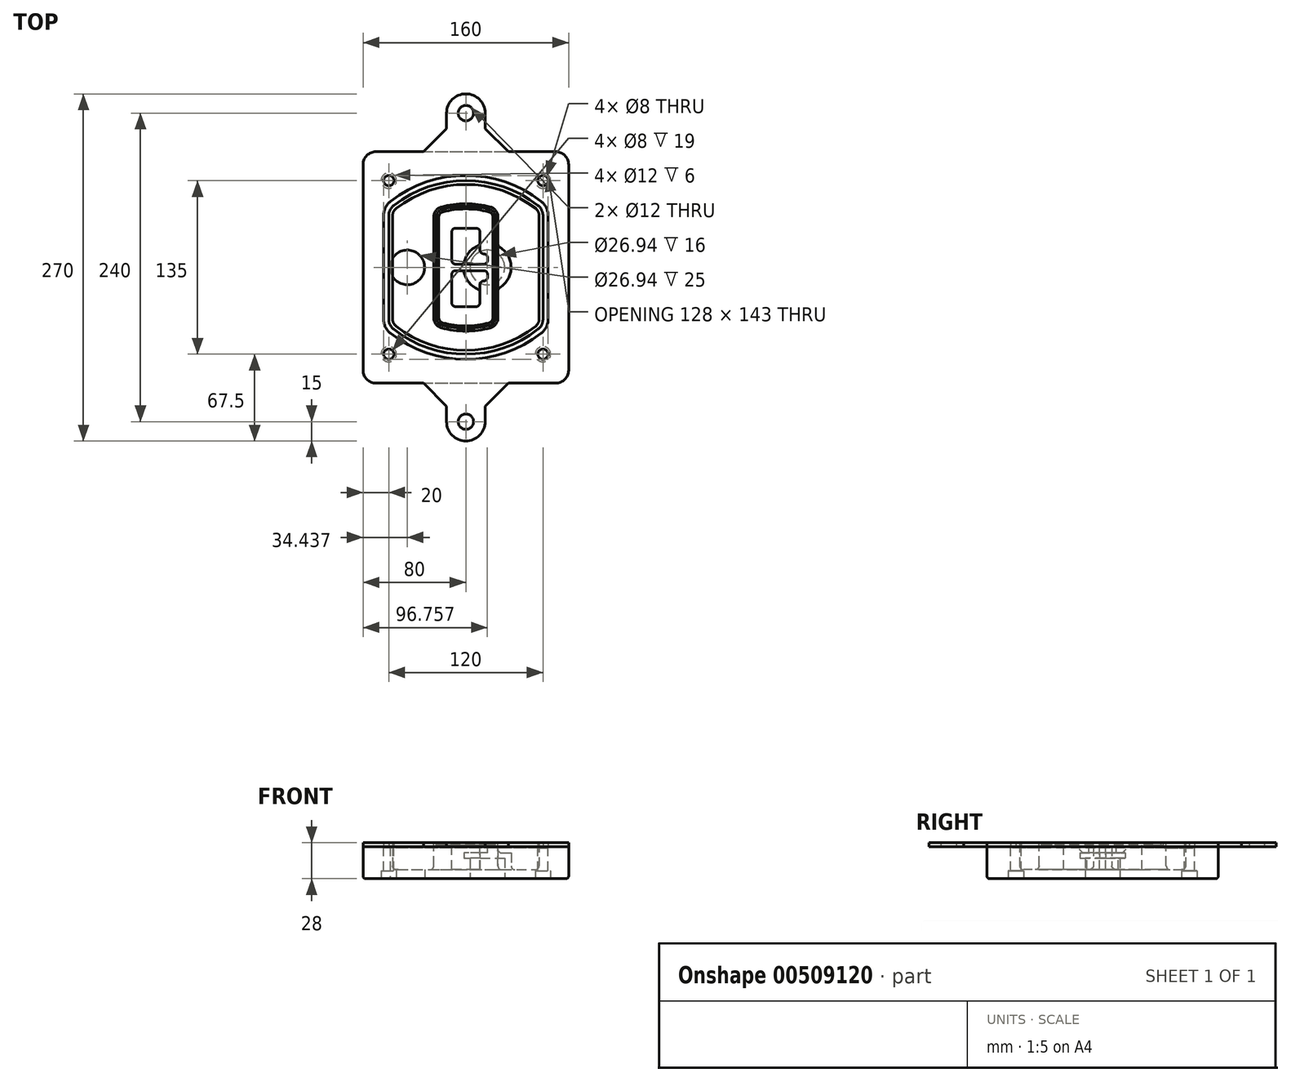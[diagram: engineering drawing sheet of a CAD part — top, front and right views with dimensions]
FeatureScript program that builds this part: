
annotation { "Feature Type Name" : "Feature", "Feature Type Description" : "" }
export const myFeature = defineFeature(function(context is Context, id is Id, definition is map)
    precondition{}
    {
        {
            var Q0;
            Q0=qCreatedBy(makeId("Top.planeOp"),FACE);
            var sketch = newSketch(context, id + "F0", { "sketchPlane" : qUnion([Q0])});
            skPoint(sketch, "E0.rect.middle", {"position": v(0, 0) * mm});
            skLineSegment(sketch, "E1.bottom", {"start": v(-70, -90) * mm, "end": v(70, -90) * mm});
            skLineSegment(sketch, "E1.top", {"start": v(-70, 90) * mm, "end": v(70, 90) * mm});
            skLineSegment(sketch, "E1.left", {"start": v(-80, -80) * mm, "end": v(-80, 80) * mm});
            skLineSegment(sketch, "E1.right", {"start": v(80, -80) * mm, "end": v(80, 80) * mm});
            skLineSegment(sketch, "E2", {"start": v(-80, 90) * mm, "end": v(80, -90) * mm, "construction": true});
            skLineSegment(sketch, "E3", {"start": v(80, 90) * mm, "end": v(-80, -90) * mm, "construction": true});
            skCircle(sketch, "E4", {"center": v(-60, 67.5) * mm, "radius": 4 * mm});
            skCircle(sketch, "E5", {"center": v(60, 67.5) * mm, "radius": 4 * mm});
            skCircle(sketch, "E6", {"center": v(60, -67.5) * mm, "radius": 4 * mm});
            skCircle(sketch, "E7", {"center": v(-60, -67.5) * mm, "radius": 4 * mm});
            skLineSegment(sketch, "E8", {"start": v(-60, 67.5) * mm, "end": v(60, 67.5) * mm, "construction": true});
            skLineSegment(sketch, "E9", {"start": v(60, 67.5) * mm, "end": v(60, -67.5) * mm, "construction": true});
            skLineSegment(sketch, "E10", {"start": v(60, -67.5) * mm, "end": v(-60, -67.5) * mm, "construction": true});
            skLineSegment(sketch, "E11", {"start": v(-60, -67.5) * mm, "end": v(-60, 67.5) * mm, "construction": true});
            skLineSegment(sketch, "E12", {"start": v(-60, 40.3) * mm, "end": v(-60, -40.3) * mm});
            skLineSegment(sketch, "E13", {"start": v(60, 40.3) * mm, "end": v(60, -40.3) * mm});
            skArc(sketch, "E14", {"start": v(56.15, 48.18) * mm, "mid": v(0, 67.5) * mm, "end": v(-56.15, 48.18) * mm});
            skArc(sketch, "E15", {"start": v(-56.15, -48.18) * mm, "mid": v(0, -67.5) * mm, "end": v(56.15, -48.18) * mm});
            skLineSegment(sketch, "E16", {"start": v(-60, 0) * mm, "end": v(60, 0) * mm, "construction": true});
            skPoint(sketch, "E17.visualSharp", {"position": v(-60, -45) * mm});
            skArc(sketch, "E17.filletArc", {"start": v(-60, -40.3) * mm, "mid": v(-58.99, -44.68) * mm, "end": v(-56.15, -48.18) * mm});
            skPoint(sketch, "E18.visualSharp", {"position": v(-60, 45) * mm});
            skArc(sketch, "E18.filletArc", {"start": v(-56.15, 48.18) * mm, "mid": v(-58.99, 44.68) * mm, "end": v(-60, 40.3) * mm});
            skPoint(sketch, "E19.visualSharp", {"position": v(60, 45) * mm});
            skArc(sketch, "E19.filletArc", {"start": v(60, 40.3) * mm, "mid": v(58.99, 44.68) * mm, "end": v(56.15, 48.18) * mm});
            skPoint(sketch, "E20.visualSharp", {"position": v(60, -45) * mm});
            skArc(sketch, "E20.filletArc", {"start": v(56.15, -48.18) * mm, "mid": v(58.99, -44.68) * mm, "end": v(60, -40.3) * mm});
            skPoint(sketch, "E21.visualSharp", {"position": v(-80, 90) * mm});
            skArc(sketch, "E21.filletArc", {"start": v(-70, 90) * mm, "mid": v(-77.07, 87.07) * mm, "end": v(-80, 80) * mm});
            skPoint(sketch, "E22.visualSharp", {"position": v(80, 90) * mm});
            skArc(sketch, "E22.filletArc", {"start": v(80, 80) * mm, "mid": v(77.07, 87.07) * mm, "end": v(70, 90) * mm});
            skPoint(sketch, "E23.visualSharp", {"position": v(80, -90) * mm});
            skArc(sketch, "E23.filletArc", {"start": v(70, -90) * mm, "mid": v(77.07, -87.07) * mm, "end": v(80, -80) * mm});
            skPoint(sketch, "E24.visualSharp", {"position": v(-80, -90) * mm});
            skArc(sketch, "E24.filletArc", {"start": v(-80, -80) * mm, "mid": v(-77.07, -87.07) * mm, "end": v(-70, -90) * mm});
            skArc(sketch, "E25.0", {"start": v(57, 40.3) * mm, "mid": v(56.3, 43.36) * mm, "end": v(54.3, 45.81) * mm});
            skLineSegment(sketch, "E25.1", {"start": v(57, 40.3) * mm, "end": v(57, -40.3) * mm});
            skArc(sketch, "E25.2", {"start": v(54.3, -45.81) * mm, "mid": v(56.3, -43.36) * mm, "end": v(57, -40.3) * mm});
            skArc(sketch, "E25.3", {"start": v(-54.3, -45.81) * mm, "mid": v(0, -64.5) * mm, "end": v(54.3, -45.81) * mm});
            skArc(sketch, "E25.4", {"start": v(-57, -40.3) * mm, "mid": v(-56.3, -43.36) * mm, "end": v(-54.3, -45.81) * mm});
            skArc(sketch, "E25.5", {"start": v(54.3, 45.81) * mm, "mid": v(0, 64.5) * mm, "end": v(-54.3, 45.81) * mm});
            skLineSegment(sketch, "E25.6", {"start": v(-57, 40.3) * mm, "end": v(-57, -40.3) * mm});
            skArc(sketch, "E25.7", {"start": v(-54.3, 45.81) * mm, "mid": v(-56.3, 43.36) * mm, "end": v(-57, 40.3) * mm});
            skArc(sketch, "E26.0", {"start": v(-58.62, 51.33) * mm, "mid": v(-62.58, 46.43) * mm, "end": v(-64, 40.3) * mm});
            skArc(sketch, "E26.1", {"start": v(58.62, 51.33) * mm, "mid": v(0, 71.5) * mm, "end": v(-58.62, 51.33) * mm});
            skArc(sketch, "E26.2", {"start": v(64, 40.3) * mm, "mid": v(62.58, 46.43) * mm, "end": v(58.62, 51.33) * mm});
            skLineSegment(sketch, "E26.3", {"start": v(64, 40.3) * mm, "end": v(64, -40.3) * mm});
            skArc(sketch, "E26.4", {"start": v(58.62, -51.33) * mm, "mid": v(62.58, -46.43) * mm, "end": v(64, -40.3) * mm});
            skLineSegment(sketch, "E26.5", {"start": v(-64, 40.3) * mm, "end": v(-64, -40.3) * mm});
            skArc(sketch, "E26.6", {"start": v(-58.62, -51.33) * mm, "mid": v(0, -71.5) * mm, "end": v(58.62, -51.33) * mm});
            skArc(sketch, "E26.7", {"start": v(-64, -40.3) * mm, "mid": v(-62.58, -46.43) * mm, "end": v(-58.62, -51.33) * mm});
            skSolve(sketch);
        }
        {
            var Q0;
            Q0=makeQuery(id+"F0.imprint","IMPRINT",FACE,{"disambiguationData":[TD([[makeQuery(id+"F0.imprint","IMPRINT",EDGE,{"derivedFrom":sQuery(id+"F0.wireOp",EDGE,"E1.bottom")}),1.0]])]});
            var Q1;
            Q1=makeQuery(id+"F0.imprint","IMPRINT",FACE,{"disambiguationData":[TD([[makeQuery(id+"F0.imprint","IMPRINT",EDGE,{"derivedFrom":sQuery(id+"F0.wireOp",EDGE,"E12")}),1.0]])]});
            var Q2;
            Q2=makeQuery(id+"F0.imprint","IMPRINT",FACE,{"disambiguationData":[TD([[makeQuery(id+"F0.imprint","IMPRINT",EDGE,{"derivedFrom":sQuery(id+"F0.wireOp",EDGE,"E25.0")}),1.0]])]});
            var Q3;
            Q3=makeQuery(id+"F0.imprint","IMPRINT",FACE,{"disambiguationData":[TD([[makeQuery(id+"F0.imprint","IMPRINT",EDGE,{"derivedFrom":sQuery(id+"F0.wireOp",EDGE,"E12")}),-1.0]])]});
            extrude(context, id + "F1", {"entities" : qUnion([Q0, Q1, Q2, Q3]), "oppositeDirection" : true, "depth" : 25 * mm});
        }
        {
            var Q0;
            Q0=makeQuery(id+"F0.imprint","IMPRINT",FACE,{"disambiguationData":[TD([[makeQuery(id+"F0.imprint","IMPRINT",EDGE,{"derivedFrom":sQuery(id+"F0.wireOp",EDGE,"E12")}),1.0]])]});
            extrude(context, id + "F2", {"entities" : qUnion([Q0]), "operationType" : NewBodyOperationType.ADD, "depth" : 3 * mm});
        }
        {
            var Q0;
            Q0=makeQuery(id+"F0.imprint","IMPRINT",FACE,{"disambiguationData":[TD([[makeQuery(id+"F0.imprint","IMPRINT",EDGE,{"derivedFrom":sQuery(id+"F0.wireOp",EDGE,"E12")}),-1.0]])]});
            extrude(context, id + "F3", {"entities" : qUnion([Q0]), "operationType" : NewBodyOperationType.REMOVE, "oppositeDirection" : true, "depth" : 1 * mm});
        }
        {
            var Q0;
            Q0=makeQuery(id+"F0.imprint","IMPRINT",FACE,{"disambiguationData":[TD([[makeQuery(id+"F0.imprint","IMPRINT",EDGE,{"derivedFrom":sQuery(id+"F0.wireOp",EDGE,"E25.0")}),1.0]])]});
            extrude(context, id + "F4", {"entities" : qUnion([Q0]), "operationType" : NewBodyOperationType.REMOVE, "oppositeDirection" : true, "depth" : 18 * mm});
        }
        {
            var Q0;
            Q0=makeQuery(id+"F2.opExtrude","CAP_FACE",FACE,{"disambiguationData":[OSD([sQuery(id+"F0.wireOp",EDGE,"E12"),sQuery(id+"F0.wireOp",EDGE,"E13"),sQuery(id+"F0.wireOp",EDGE,"E14"),sQuery(id+"F0.wireOp",EDGE,"E15"),sQuery(id+"F0.wireOp",EDGE,"E17.filletArc"),sQuery(id+"F0.wireOp",EDGE,"E18.filletArc"),sQuery(id+"F0.wireOp",EDGE,"E19.filletArc"),sQuery(id+"F0.wireOp",EDGE,"E20.filletArc"),sQuery(id+"F0.wireOp",EDGE,"E25.0"),sQuery(id+"F0.wireOp",EDGE,"E25.1"),sQuery(id+"F0.wireOp",EDGE,"E25.2"),sQuery(id+"F0.wireOp",EDGE,"E25.3"),sQuery(id+"F0.wireOp",EDGE,"E25.4"),sQuery(id+"F0.wireOp",EDGE,"E25.5"),sQuery(id+"F0.wireOp",EDGE,"E25.6"),sQuery(id+"F0.wireOp",EDGE,"E25.7")])],"isStart":false});
            var sketch = newSketch(context, id + "F5", { "sketchPlane" : qUnion([Q0])});
            skArc(sketch, "E27.0", {"start": v(-19.08, -46.97) * mm, "mid": v(0, -49.5) * mm, "end": v(19.08, -46.97) * mm});
            skArc(sketch, "E28.0", {"start": v(19.08, 46.97) * mm, "mid": v(0, 49.5) * mm, "end": v(-19.08, 46.97) * mm});
            skLineSegment(sketch, "E29", {"start": v(-25, 39.25) * mm, "end": v(-25, -39.25) * mm});
            skLineSegment(sketch, "E30", {"start": v(25, 39.25) * mm, "end": v(25, -39.25) * mm});
            skLineSegment(sketch, "E31", {"start": v(-25, 45.1) * mm, "end": v(25, 45.1) * mm, "construction": true});
            skLineSegment(sketch, "E32", {"start": v(-25, -45.1) * mm, "end": v(25, -45.1) * mm, "construction": true});
            skPoint(sketch, "E33.visualSharp", {"position": v(-25, 45.1) * mm});
            skArc(sketch, "E33.filletArc", {"start": v(-19.08, 46.97) * mm, "mid": v(-23.35, 44.11) * mm, "end": v(-25, 39.25) * mm});
            skPoint(sketch, "E34.visualSharp", {"position": v(25, 45.1) * mm});
            skArc(sketch, "E34.filletArc", {"start": v(25, 39.25) * mm, "mid": v(23.35, 44.11) * mm, "end": v(19.08, 46.97) * mm});
            skPoint(sketch, "E35.visualSharp", {"position": v(25, -45.1) * mm});
            skArc(sketch, "E35.filletArc", {"start": v(19.08, -46.97) * mm, "mid": v(23.35, -44.11) * mm, "end": v(25, -39.25) * mm});
            skPoint(sketch, "E36.visualSharp", {"position": v(-25, -45.1) * mm});
            skArc(sketch, "E36.filletArc", {"start": v(-25, -39.25) * mm, "mid": v(-23.35, -44.11) * mm, "end": v(-19.08, -46.97) * mm});
            skArc(sketch, "E37.0", {"start": v(54.3, 45.81) * mm, "mid": v(0, 64.5) * mm, "end": v(-54.3, 45.81) * mm});
            skArc(sketch, "E37.1", {"start": v(-54.3, 45.81) * mm, "mid": v(-56.3, 43.36) * mm, "end": v(-57, 40.3) * mm});
            skLineSegment(sketch, "E37.2", {"start": v(-57, 40.3) * mm, "end": v(-57, -40.3) * mm});
            skArc(sketch, "E37.3", {"start": v(-57, -40.3) * mm, "mid": v(-56.3, -43.36) * mm, "end": v(-54.3, -45.81) * mm});
            skArc(sketch, "E37.4", {"start": v(-54.3, -45.81) * mm, "mid": v(0, -64.5) * mm, "end": v(54.3, -45.81) * mm});
            skArc(sketch, "E37.5", {"start": v(54.3, -45.81) * mm, "mid": v(56.3, -43.36) * mm, "end": v(57, -40.3) * mm});
            skLineSegment(sketch, "E37.6", {"start": v(57, 40.3) * mm, "end": v(57, -40.3) * mm});
            skArc(sketch, "E37.7", {"start": v(57, 40.3) * mm, "mid": v(56.3, 43.36) * mm, "end": v(54.3, 45.81) * mm});
            skLineSegment(sketch, "E38.0", {"start": v(23, 39.25) * mm, "end": v(23, -39.25) * mm});
            skArc(sketch, "E38.1", {"start": v(18.56, -45.04) * mm, "mid": v(21.76, -42.9) * mm, "end": v(23, -39.25) * mm});
            skArc(sketch, "E38.2", {"start": v(-18.56, -45.04) * mm, "mid": v(0, -47.5) * mm, "end": v(18.56, -45.04) * mm});
            skArc(sketch, "E38.3", {"start": v(-23, -39.25) * mm, "mid": v(-21.76, -42.9) * mm, "end": v(-18.56, -45.04) * mm});
            skLineSegment(sketch, "E38.4", {"start": v(-23, 39.25) * mm, "end": v(-23, -39.25) * mm});
            skArc(sketch, "E38.5", {"start": v(23, 39.25) * mm, "mid": v(21.76, 42.9) * mm, "end": v(18.56, 45.04) * mm});
            skArc(sketch, "E38.6", {"start": v(-18.56, 45.04) * mm, "mid": v(-21.76, 42.9) * mm, "end": v(-23, 39.25) * mm});
            skArc(sketch, "E38.7", {"start": v(18.56, 45.04) * mm, "mid": v(0, 47.5) * mm, "end": v(-18.56, 45.04) * mm});
            skArc(sketch, "E39.0", {"start": v(21, 39.25) * mm, "mid": v(20.18, 41.68) * mm, "end": v(18.04, 43.1) * mm});
            skLineSegment(sketch, "E39.1", {"start": v(21, 39.25) * mm, "end": v(21, -39.25) * mm});
            skArc(sketch, "E39.2", {"start": v(18.04, -43.1) * mm, "mid": v(20.18, -41.68) * mm, "end": v(21, -39.25) * mm});
            skArc(sketch, "E39.3", {"start": v(-18.04, -43.1) * mm, "mid": v(0, -45.5) * mm, "end": v(18.04, -43.1) * mm});
            skArc(sketch, "E39.4", {"start": v(-21, -39.25) * mm, "mid": v(-20.18, -41.68) * mm, "end": v(-18.04, -43.1) * mm});
            skArc(sketch, "E39.5", {"start": v(18.04, 43.1) * mm, "mid": v(0, 45.5) * mm, "end": v(-18.04, 43.1) * mm});
            skLineSegment(sketch, "E39.6", {"start": v(-21, 39.25) * mm, "end": v(-21, -39.25) * mm});
            skArc(sketch, "E39.7", {"start": v(-18.04, 43.1) * mm, "mid": v(-20.18, 41.68) * mm, "end": v(-21, 39.25) * mm});
            skLineSegment(sketch, "E40", {"start": v(-25, 0) * mm, "end": v(25, 0) * mm, "construction": true});
            skLineSegment(sketch, "E41", {"start": v(-11, 5.5) * mm, "end": v(-11, 27.5) * mm});
            skLineSegment(sketch, "E42", {"start": v(-8, 30.5) * mm, "end": v(8, 30.5) * mm});
            skLineSegment(sketch, "E43", {"start": v(11, 27.5) * mm, "end": v(11, 13.5) * mm});
            skLineSegment(sketch, "E44", {"start": v(14, 10.5) * mm, "end": v(14, 10.5) * mm});
            skLineSegment(sketch, "E45", {"start": v(17, 7.5) * mm, "end": v(17, 5.5) * mm});
            skLineSegment(sketch, "E46", {"start": v(14, 2.5) * mm, "end": v(-8, 2.5) * mm});
            skPoint(sketch, "E47.visualSharp", {"position": v(-11, 30.5) * mm});
            skArc(sketch, "E47.filletArc", {"start": v(-8, 30.5) * mm, "mid": v(-10.12, 29.62) * mm, "end": v(-11, 27.5) * mm});
            skPoint(sketch, "E48.visualSharp", {"position": v(11, 30.5) * mm});
            skArc(sketch, "E48.filletArc", {"start": v(11, 27.5) * mm, "mid": v(10.12, 29.62) * mm, "end": v(8, 30.5) * mm});
            skPoint(sketch, "E49.visualSharp", {"position": v(11, 10.5) * mm});
            skArc(sketch, "E49.filletArc", {"start": v(11, 13.5) * mm, "mid": v(11.88, 11.38) * mm, "end": v(14, 10.5) * mm});
            skPoint(sketch, "E50.visualSharp", {"position": v(17, 10.5) * mm});
            skArc(sketch, "E50.filletArc", {"start": v(17, 7.5) * mm, "mid": v(16.12, 9.62) * mm, "end": v(14, 10.5) * mm});
            skPoint(sketch, "E51.visualSharp", {"position": v(17, 2.5) * mm});
            skArc(sketch, "E51.filletArc", {"start": v(14, 2.5) * mm, "mid": v(16.12, 3.38) * mm, "end": v(17, 5.5) * mm});
            skPoint(sketch, "E52.visualSharp", {"position": v(-11, 2.5) * mm});
            skArc(sketch, "E52.filletArc", {"start": v(-11, 5.5) * mm, "mid": v(-10.12, 3.38) * mm, "end": v(-8, 2.5) * mm});
            skLineSegment(sketch, "E53.0.MirrorCS", {"start": v(14, -2.5) * mm, "end": v(-8, -2.5) * mm});
            skArc(sketch, "E54.0.MirrorCS", {"start": v(-11, -5.5) * mm, "mid": v(-10.12, -3.38) * mm, "end": v(-8, -2.5) * mm});
            skLineSegment(sketch, "E55.0.MirrorCS", {"start": v(-11, -5.5) * mm, "end": v(-11, -27.5) * mm});
            skArc(sketch, "E56.0.MirrorCS", {"start": v(-8, -30.5) * mm, "mid": v(-10.12, -29.62) * mm, "end": v(-11, -27.5) * mm});
            skLineSegment(sketch, "E57.0.MirrorCS", {"start": v(-8, -30.5) * mm, "end": v(8, -30.5) * mm});
            skArc(sketch, "E58.0.MirrorCS", {"start": v(11, -27.5) * mm, "mid": v(10.12, -29.62) * mm, "end": v(8, -30.5) * mm});
            skLineSegment(sketch, "E59.0.MirrorCS", {"start": v(11, -27.5) * mm, "end": v(11, -13.5) * mm});
            skArc(sketch, "E60.0.MirrorCS", {"start": v(11, -13.5) * mm, "mid": v(11.88, -11.38) * mm, "end": v(14, -10.5) * mm});
            skArc(sketch, "E61.0.MirrorCS", {"start": v(17, -7.5) * mm, "mid": v(16.12, -9.62) * mm, "end": v(14, -10.5) * mm});
            skLineSegment(sketch, "E62.0.MirrorCS", {"start": v(17, -7.5) * mm, "end": v(17, -5.5) * mm});
            skArc(sketch, "E63.0.MirrorCS", {"start": v(14, -2.5) * mm, "mid": v(16.12, -3.38) * mm, "end": v(17, -5.5) * mm});
            skSolve(sketch);
        }
        {
            var Q0;
            Q0=makeQuery(id+"F5.imprint","IMPRINT",FACE,{"disambiguationData":[TD([[makeQuery(id+"F5.imprint","IMPRINT",EDGE,{"derivedFrom":sQuery(id+"F5.wireOp",EDGE,"E27.0")}),1.0]])]});
            var Q1;
            Q1=makeQuery(id+"F5.imprint","IMPRINT",FACE,{"disambiguationData":[TD([[makeQuery(id+"F5.imprint","IMPRINT",EDGE,{"derivedFrom":sQuery(id+"F5.wireOp",EDGE,"E38.0")}),-1.0]])]});
            var Q2;
            Q2=makeQuery(id+"F5.imprint","IMPRINT",FACE,{"disambiguationData":[TD([[makeQuery(id+"F5.imprint","IMPRINT",EDGE,{"derivedFrom":sQuery(id+"F5.wireOp",EDGE,"E39.0")}),1.0]])]});
            extrude(context, id + "F6", {"entities" : qUnion([Q0, Q1, Q2]), "operationType" : NewBodyOperationType.ADD, "endBound" : BoundingType.UP_TO_NEXT, "oppositeDirection" : true, "depth" : 25 * mm});
        }
        {
            var Q0;
            Q0=makeQuery(id+"F5.imprint","IMPRINT",FACE,{"disambiguationData":[TD([[makeQuery(id+"F5.imprint","IMPRINT",EDGE,{"derivedFrom":sQuery(id+"F5.wireOp",EDGE,"E38.0")}),-1.0]])]});
            extrude(context, id + "F7", {"entities" : qUnion([Q0]), "operationType" : NewBodyOperationType.REMOVE, "oppositeDirection" : true, "depth" : 2 * mm});
        }
        {
            var Q0;
            Q0=makeQuery(id+"F1.opExtrude","CAP_FACE",FACE,{"disambiguationData":[OSD([sQuery(id+"F0.wireOp",EDGE,"E1.bottom"),sQuery(id+"F0.wireOp",EDGE,"E1.top"),sQuery(id+"F0.wireOp",EDGE,"E1.left"),sQuery(id+"F0.wireOp",EDGE,"E1.right"),sQuery(id+"F0.wireOp",EDGE,"E4"),sQuery(id+"F0.wireOp",EDGE,"E5"),sQuery(id+"F0.wireOp",EDGE,"E6"),sQuery(id+"F0.wireOp",EDGE,"E7"),sQuery(id+"F0.wireOp",EDGE,"E21.filletArc"),sQuery(id+"F0.wireOp",EDGE,"E22.filletArc"),sQuery(id+"F0.wireOp",EDGE,"E23.filletArc"),sQuery(id+"F0.wireOp",EDGE,"E24.filletArc")])],"isStart":false});
            var sketch = newSketch(context, id + "F8", { "sketchPlane" : qUnion([Q0])});
            skCircle(sketch, "E64", {"center": v(16.76, 0) * mm, "radius": 13.47 * mm});
            skCircle(sketch, "E65", {"center": v(-45.56, 0) * mm, "radius": 13.47 * mm});
            skLineSegment(sketch, "E66", {"start": v(80, 0) * mm, "end": v(-80, 0) * mm});
            skCircle(sketch, "E67", {"center": v(16.76, 0) * mm, "radius": 18.47 * mm});
            skCircle(sketch, "E68", {"center": v(60, -67.5) * mm, "radius": 6 * mm});
            skCircle(sketch, "E69", {"center": v(-60, -67.5) * mm, "radius": 6 * mm});
            skCircle(sketch, "E70", {"center": v(-60, 67.5) * mm, "radius": 6 * mm});
            skCircle(sketch, "E71", {"center": v(60, 67.5) * mm, "radius": 6 * mm});
            skSolve(sketch);
        }
        {
            var Q0;
            {var subQ1=sQuery(id+"F8.wireOp",EDGE,"E66");var subQ4=sQuery(id+"F8.wireOp",EDGE,"E64");var subQ6=makeQuery(id+"F8.imprint","INTERSECT",VERTEX,{"disambiguationData":[OD(0.0)],"derivedFrom":[subQ4,subQ1]});Q0=makeQuery(id+"F8.imprint","IMPRINT",FACE,{"disambiguationData":[TD([[makeQuery(id+"F8.imprint","IMPRINT",EDGE,{"disambiguationData":[TD([[subQ6,-1.0]])],"derivedFrom":subQ4}),-1.0]])]});}
            var Q1;
            {var subQ0=sQuery(id+"F8.wireOp",EDGE,"E66");var subQ1=sQuery(id+"F8.wireOp",EDGE,"E64");var subQ3=makeQuery(id+"F8.imprint","INTERSECT",VERTEX,{"disambiguationData":[OD(0.0)],"derivedFrom":[subQ1,subQ0]});Q1=makeQuery(id+"F8.imprint","IMPRINT",FACE,{"disambiguationData":[TD([[makeQuery(id+"F8.imprint","IMPRINT",EDGE,{"disambiguationData":[TD([[subQ3,-1.0]])],"derivedFrom":subQ1}),1.0]])]});}
            var Q2;
            {var subQ0=sQuery(id+"F8.wireOp",EDGE,"E66");var subQ1=sQuery(id+"F8.wireOp",EDGE,"E64");var subQ3=makeQuery(id+"F8.imprint","INTERSECT",VERTEX,{"disambiguationData":[OD(0.0)],"derivedFrom":[subQ1,subQ0]});Q2=makeQuery(id+"F8.imprint","IMPRINT",FACE,{"disambiguationData":[TD([[makeQuery(id+"F8.imprint","IMPRINT",EDGE,{"disambiguationData":[TD([[subQ3,1.0]])],"derivedFrom":subQ1}),1.0]])]});}
            var Q3;
            {var subQ1=sQuery(id+"F8.wireOp",EDGE,"E66");var subQ4=sQuery(id+"F8.wireOp",EDGE,"E64");var subQ6=makeQuery(id+"F8.imprint","INTERSECT",VERTEX,{"disambiguationData":[OD(0.0)],"derivedFrom":[subQ4,subQ1]});Q3=makeQuery(id+"F8.imprint","IMPRINT",FACE,{"disambiguationData":[TD([[makeQuery(id+"F8.imprint","IMPRINT",EDGE,{"disambiguationData":[TD([[subQ6,1.0]])],"derivedFrom":subQ4}),-1.0]])]});}
            extrude(context, id + "F9", {"entities" : qUnion([Q0, Q1, Q2, Q3]), "operationType" : NewBodyOperationType.ADD, "oppositeDirection" : true, "depth" : 20 * mm});
        }
        {
            var Q0;
            {var subQ0=sQuery(id+"F8.wireOp",EDGE,"E66");var subQ1=sQuery(id+"F8.wireOp",EDGE,"E64");var subQ3=makeQuery(id+"F8.imprint","INTERSECT",VERTEX,{"disambiguationData":[OD(0.0)],"derivedFrom":[subQ1,subQ0]});Q0=makeQuery(id+"F8.imprint","IMPRINT",FACE,{"disambiguationData":[TD([[makeQuery(id+"F8.imprint","IMPRINT",EDGE,{"disambiguationData":[TD([[subQ3,-1.0]])],"derivedFrom":subQ1}),1.0]])]});}
            var Q1;
            {var subQ0=sQuery(id+"F8.wireOp",EDGE,"E66");var subQ1=sQuery(id+"F8.wireOp",EDGE,"E64");var subQ3=makeQuery(id+"F8.imprint","INTERSECT",VERTEX,{"disambiguationData":[OD(0.0)],"derivedFrom":[subQ1,subQ0]});Q1=makeQuery(id+"F8.imprint","IMPRINT",FACE,{"disambiguationData":[TD([[makeQuery(id+"F8.imprint","IMPRINT",EDGE,{"disambiguationData":[TD([[subQ3,1.0]])],"derivedFrom":subQ1}),1.0]])]});}
            extrude(context, id + "F10", {"entities" : qUnion([Q0, Q1]), "operationType" : NewBodyOperationType.REMOVE, "oppositeDirection" : true, "depth" : 16 * mm});
        }
        {
            var Q0;
            {var subQ0=sQuery(id+"F8.wireOp",EDGE,"E66");var subQ1=sQuery(id+"F8.wireOp",EDGE,"E65");var subQ3=makeQuery(id+"F8.imprint","INTERSECT",VERTEX,{"disambiguationData":[OD(0.0)],"derivedFrom":[subQ1,subQ0]});Q0=makeQuery(id+"F8.imprint","IMPRINT",FACE,{"disambiguationData":[TD([[makeQuery(id+"F8.imprint","IMPRINT",EDGE,{"disambiguationData":[TD([[subQ3,-1.0]])],"derivedFrom":subQ1}),1.0]])]});}
            var Q1;
            {var subQ0=sQuery(id+"F8.wireOp",EDGE,"E66");var subQ1=sQuery(id+"F8.wireOp",EDGE,"E65");var subQ3=makeQuery(id+"F8.imprint","INTERSECT",VERTEX,{"disambiguationData":[OD(0.0)],"derivedFrom":[subQ1,subQ0]});Q1=makeQuery(id+"F8.imprint","IMPRINT",FACE,{"disambiguationData":[TD([[makeQuery(id+"F8.imprint","IMPRINT",EDGE,{"disambiguationData":[TD([[subQ3,1.0]])],"derivedFrom":subQ1}),1.0]])]});}
            extrude(context, id + "F11", {"entities" : qUnion([Q0, Q1]), "operationType" : NewBodyOperationType.REMOVE, "oppositeDirection" : true, "depth" : 25 * mm});
        }
        {
            var Q0;
            Q0=makeQuery(id+"F8.imprint","IMPRINT",FACE,{"disambiguationData":[TD([[makeQuery(id+"F8.imprint","IMPRINT",EDGE,{"derivedFrom":sQuery(id+"F8.wireOp",EDGE,"E68")}),1.0]])]});
            var Q1;
            Q1=makeQuery(id+"F8.imprint","IMPRINT",FACE,{"disambiguationData":[TD([[makeQuery(id+"F8.imprint","IMPRINT",EDGE,{"derivedFrom":makeQuery(id+"F1.opExtrude","CAP_EDGE",EDGE,{"disambiguationData":[OSD([sQuery(id+"F0.wireOp",EDGE,"E5")])],"isStart":false})}),-1.0]])]});
            var Q2;
            Q2=makeQuery(id+"F8.imprint","IMPRINT",FACE,{"disambiguationData":[TD([[makeQuery(id+"F8.imprint","IMPRINT",EDGE,{"derivedFrom":sQuery(id+"F8.wireOp",EDGE,"E69")}),1.0]])]});
            var Q3;
            Q3=makeQuery(id+"F8.imprint","IMPRINT",FACE,{"disambiguationData":[TD([[makeQuery(id+"F8.imprint","IMPRINT",EDGE,{"derivedFrom":makeQuery(id+"F1.opExtrude","CAP_EDGE",EDGE,{"disambiguationData":[OSD([sQuery(id+"F0.wireOp",EDGE,"E4")])],"isStart":false})}),-1.0]])]});
            var Q4;
            Q4=makeQuery(id+"F8.imprint","IMPRINT",FACE,{"disambiguationData":[TD([[makeQuery(id+"F8.imprint","IMPRINT",EDGE,{"derivedFrom":sQuery(id+"F8.wireOp",EDGE,"E70")}),1.0]])]});
            var Q5;
            Q5=makeQuery(id+"F8.imprint","IMPRINT",FACE,{"disambiguationData":[TD([[makeQuery(id+"F8.imprint","IMPRINT",EDGE,{"derivedFrom":makeQuery(id+"F1.opExtrude","CAP_EDGE",EDGE,{"disambiguationData":[OSD([sQuery(id+"F0.wireOp",EDGE,"E7")])],"isStart":false})}),-1.0]])]});
            var Q6;
            Q6=makeQuery(id+"F8.imprint","IMPRINT",FACE,{"disambiguationData":[TD([[makeQuery(id+"F8.imprint","IMPRINT",EDGE,{"derivedFrom":sQuery(id+"F8.wireOp",EDGE,"E71")}),1.0]])]});
            var Q7;
            Q7=makeQuery(id+"F8.imprint","IMPRINT",FACE,{"disambiguationData":[TD([[makeQuery(id+"F8.imprint","IMPRINT",EDGE,{"derivedFrom":makeQuery(id+"F1.opExtrude","CAP_EDGE",EDGE,{"disambiguationData":[OSD([sQuery(id+"F0.wireOp",EDGE,"E6")])],"isStart":false})}),-1.0]])]});
            extrude(context, id + "F12", {"entities" : qUnion([Q0, Q1, Q2, Q3, Q4, Q5, Q6, Q7]), "operationType" : NewBodyOperationType.REMOVE, "oppositeDirection" : true, "depth" : 6 * mm});
        }
        {
            var Q0;
            Q0=makeQuery(id+"F10.boolean.opBoolean","COPY",FACE,{"derivedFrom":makeQuery(id+"F10.opExtrude","CAP_FACE",FACE,{"disambiguationData":[OSD([sQuery(id+"F8.wireOp",EDGE,"E64")])],"isStart":false})});
            var sketch = newSketch(context, id + "F13", { "sketchPlane" : qUnion([Q0])});
            skArc(sketch, "E72.0", {"start": v(11, 17.55) * mm, "mid": v(2.57, 11.82) * mm, "end": v(-1.54, 2.5) * mm});
            skArc(sketch, "E72.1", {"start": v(-1.54, -2.5) * mm, "mid": v(2.57, -11.82) * mm, "end": v(11, -17.55) * mm});
            skLineSegment(sketch, "E73", {"start": v(-1.54, -2.5) * mm, "end": v(14, -2.5) * mm});
            skLineSegment(sketch, "E74.0", {"start": v(14, 2.5) * mm, "end": v(-1.54, 2.5) * mm});
            skArc(sketch, "E74.1", {"start": v(14, 2.5) * mm, "mid": v(16.12, 3.38) * mm, "end": v(17, 5.5) * mm});
            skLineSegment(sketch, "E74.2", {"start": v(17, 7.5) * mm, "end": v(17, 5.5) * mm});
            skArc(sketch, "E74.3", {"start": v(17, 7.5) * mm, "mid": v(16.12, 9.62) * mm, "end": v(14, 10.5) * mm});
            skArc(sketch, "E74.4", {"start": v(11, 13.5) * mm, "mid": v(11.88, 11.38) * mm, "end": v(14, 10.5) * mm});
            skLineSegment(sketch, "E74.5", {"start": v(11, 17.55) * mm, "end": v(11, 13.5) * mm});
            skLineSegment(sketch, "E74.7", {"start": v(14, -2.5) * mm, "end": v(-1.54, -2.5) * mm});
            skArc(sketch, "E74.8", {"start": v(14, -2.5) * mm, "mid": v(16.12, -3.38) * mm, "end": v(17, -5.5) * mm});
            skLineSegment(sketch, "E74.9", {"start": v(17, -7.5) * mm, "end": v(17, -5.5) * mm});
            skArc(sketch, "E74.10", {"start": v(17, -7.5) * mm, "mid": v(16.12, -9.62) * mm, "end": v(14, -10.5) * mm});
            skArc(sketch, "E74.11", {"start": v(11, -13.5) * mm, "mid": v(11.88, -11.38) * mm, "end": v(14, -10.5) * mm});
            skLineSegment(sketch, "E74.12", {"start": v(11, -17.55) * mm, "end": v(11, -13.5) * mm});
            skPoint(sketch, "E75.orphan", {"position": v(11, -27.5) * mm});
            skPoint(sketch, "E76.orphan", {"position": v(-8, -2.5) * mm});
            skPoint(sketch, "E77.orphan", {"position": v(-8, 2.5) * mm});
            skPoint(sketch, "E78.orphan", {"position": v(11, 27.5) * mm});
            skSolve(sketch);
        }
        {
            var Q0;
            {var subQ7=sQuery(id+"F13.wireOp",EDGE,"E72.0");var subQ14=sQuery(id+"F13.wireOp",EDGE,"E72.1");var subQ16=sQuery(id+"F13.wireOp",EDGE,"E74.1");var subQ18=sQuery(id+"F13.wireOp",EDGE,"E74.8");Q0=qUnion([makeQuery(id+"F13.imprint","IMPRINT",FACE,{"disambiguationData":[TD([[makeQuery(id+"F13.imprint","IMPRINT",EDGE,{"derivedFrom":subQ7}),1.0]])]}),makeQuery(id+"F13.imprint","IMPRINT",FACE,{"disambiguationData":[TD([[makeQuery(id+"F13.imprint","IMPRINT",EDGE,{"derivedFrom":subQ14}),1.0]])]}),makeQuery(id+"F13.imprint","IMPRINT",FACE,{"disambiguationData":[TD([[makeQuery(id+"F13.imprint","IMPRINT",EDGE,{"derivedFrom":subQ16}),1.0]])]}),makeQuery(id+"F13.imprint","IMPRINT",FACE,{"disambiguationData":[TD([[makeQuery(id+"F13.imprint","IMPRINT",EDGE,{"derivedFrom":subQ18}),-1.0]])]})]);}
            var Q1;
            Q1=makeQuery(id+"F6.boolean.opBoolean","SPLIT",FACE,{"disambiguationData":[TD([makeQuery(id+"F6.opExtrude","SWEPT_FACE",FACE,{"disambiguationData":[OSD([sQuery(id+"F5.wireOp",EDGE,"E41")])]})])],"derivedFrom":makeQuery(id+"F4.boolean.opBoolean","COPY",FACE,{"derivedFrom":makeQuery(id+"F4.opExtrude","CAP_FACE",FACE,{"disambiguationData":[OSD([sQuery(id+"F0.wireOp",EDGE,"E25.0"),sQuery(id+"F0.wireOp",EDGE,"E25.1"),sQuery(id+"F0.wireOp",EDGE,"E25.2"),sQuery(id+"F0.wireOp",EDGE,"E25.3"),sQuery(id+"F0.wireOp",EDGE,"E25.4"),sQuery(id+"F0.wireOp",EDGE,"E25.5"),sQuery(id+"F0.wireOp",EDGE,"E25.6"),sQuery(id+"F0.wireOp",EDGE,"E25.7")])],"isStart":false})})});
            extrude(context, id + "F14", {"entities" : qUnion([Q0]), "operationType" : NewBodyOperationType.REMOVE, "endBound" : BoundingType.UP_TO_SURFACE, "endBoundEntityFace" : qUnion([Q1]), "depth" : 25 * mm});
        }
        {
            var Q0;
            Q0=makeQuery(id+"F4.boolean.opBoolean","COPY",EDGE,{"derivedFrom":makeQuery(id+"F4.opExtrude","CAP_EDGE",EDGE,{"disambiguationData":[OSD([sQuery(id+"F0.wireOp",EDGE,"E25.6")])],"isStart":false})});
            var Q1;
            Q1=makeQuery(id+"F9.boolean.opBoolean","INTERSECT",EDGE,{"derivedFrom":[makeQuery(id+"F6.opExtrude","SWEPT_FACE",FACE,{"disambiguationData":[OSD([sQuery(id+"F5.wireOp",EDGE,"E30")])]}),makeQuery(id+"F9.opExtrude","CAP_FACE",FACE,{"disambiguationData":[OSD([sQuery(id+"F8.wireOp",EDGE,"E67")])],"isStart":false})]});
            var Q2;
            Q2=makeQuery(id+"F9.boolean.opBoolean","INTERSECT",EDGE,{"disambiguationData":[OD(1.0)],"derivedFrom":[makeQuery(id+"F6.opExtrude","SWEPT_FACE",FACE,{"disambiguationData":[OSD([sQuery(id+"F5.wireOp",EDGE,"E30")])]}),makeQuery(id+"F9.opExtrude","SWEPT_FACE",FACE,{"disambiguationData":[OSD([sQuery(id+"F8.wireOp",EDGE,"E67")])]})]});
            var Q3;
            {var subQ0=sQuery(id+"F5.wireOp",EDGE,"E30");Q3=makeQuery(id+"F9.boolean.opBoolean","SPLIT",EDGE,{"disambiguationData":[TD([makeQuery(id+"F6.opExtrude","SWEPT_FACE",FACE,{"disambiguationData":[OSD([sQuery(id+"F5.wireOp",EDGE,"E35.filletArc")])]})])],"derivedFrom":makeQuery(id+"F6.opExtrude","CAP_EDGE",EDGE,{"disambiguationData":[OSD([subQ0])],"isStart":false})});}
            var Q4;
            {var subQ0=sQuery(id+"F0.wireOp",EDGE,"E25.7");var subQ1=sQuery(id+"F0.wireOp",EDGE,"E25.6");var subQ2=sQuery(id+"F0.wireOp",EDGE,"E25.5");var subQ3=sQuery(id+"F0.wireOp",EDGE,"E25.4");var subQ4=sQuery(id+"F0.wireOp",EDGE,"E25.0");var subQ5=sQuery(id+"F0.wireOp",EDGE,"E25.1");var subQ6=sQuery(id+"F0.wireOp",EDGE,"E25.2");var subQ7=sQuery(id+"F0.wireOp",EDGE,"E25.3");Q4=makeQuery(id+"F9.boolean.opBoolean","INTERSECT",EDGE,{"derivedFrom":[makeQuery(id+"F6.boolean.opBoolean","SPLIT",FACE,{"disambiguationData":[TD([makeQuery(id+"F2.opExtrude","SWEPT_FACE",FACE,{"disambiguationData":[OSD([subQ4])]})])],"derivedFrom":makeQuery(id+"F4.boolean.opBoolean","COPY",FACE,{"derivedFrom":makeQuery(id+"F4.opExtrude","CAP_FACE",FACE,{"disambiguationData":[OSD([subQ4,subQ5,subQ6,subQ7,subQ3,subQ2,subQ1,subQ0])],"isStart":false})})}),makeQuery(id+"F9.opExtrude","SWEPT_FACE",FACE,{"disambiguationData":[OSD([sQuery(id+"F8.wireOp",EDGE,"E67")])]})]});}
            var Q5;
            Q5=makeQuery(id+"F9.boolean.opBoolean","INTERSECT",EDGE,{"disambiguationData":[OD(0.0)],"derivedFrom":[makeQuery(id+"F6.opExtrude","SWEPT_FACE",FACE,{"disambiguationData":[OSD([sQuery(id+"F5.wireOp",EDGE,"E30")])]}),makeQuery(id+"F9.opExtrude","SWEPT_FACE",FACE,{"disambiguationData":[OSD([sQuery(id+"F8.wireOp",EDGE,"E67")])]})]});
            fillet(context, id + "F15", {"entities" : qUnion([Q0, Q1, Q2, Q3, Q4, Q5]), "radius" : 3 * mm, "tangentPropagation" : true, "allowEdgeOverflow" : false});
        }
        {
            var Q0;
            Q0=makeQuery(id+"F1.opExtrude","CAP_EDGE",EDGE,{"disambiguationData":[OSD([sQuery(id+"F0.wireOp",EDGE,"E1.bottom")])],"isStart":false});
            fillet(context, id + "F16", {"entities" : qUnion([Q0]), "radius" : 2 * mm, "tangentPropagation" : true, "allowEdgeOverflow" : false});
        }
        {
            var Q0;
            {var subQ0=sQuery(id+"F0.wireOp",EDGE,"E21.filletArc");var subQ1=sQuery(id+"F0.wireOp",EDGE,"E7");var subQ2=sQuery(id+"F0.wireOp",EDGE,"E6");var subQ3=sQuery(id+"F0.wireOp",EDGE,"E5");var subQ4=sQuery(id+"F0.wireOp",EDGE,"E4");var subQ5=sQuery(id+"F0.wireOp",EDGE,"E22.filletArc");var subQ6=sQuery(id+"F0.wireOp",EDGE,"E1.bottom");var subQ7=sQuery(id+"F0.wireOp",EDGE,"E1.right");var subQ8=sQuery(id+"F0.wireOp",EDGE,"E1.top");var subQ9=sQuery(id+"F0.wireOp",EDGE,"E1.left");var subQ10=sQuery(id+"F0.wireOp",EDGE,"E23.filletArc");var subQ11=sQuery(id+"F0.wireOp",EDGE,"E24.filletArc");Q0=makeQuery(id+"F2.boolean.opBoolean","SPLIT",FACE,{"disambiguationData":[TD([makeQuery(id+"F1.opExtrude","SWEPT_FACE",FACE,{"disambiguationData":[OSD([subQ6])]})])],"derivedFrom":makeQuery(id+"F1.opExtrude","CAP_FACE",FACE,{"disambiguationData":[OSD([subQ6,subQ8,subQ9,subQ7,subQ4,subQ3,subQ2,subQ1,subQ0,subQ5,subQ10,subQ11])],"isStart":true})});}
            var sketch = newSketch(context, id + "F17", { "sketchPlane" : qUnion([Q0])});
            skPoint(sketch, "E79.endSnap0", {"position": v(80, 0) * mm});
            skArc(sketch, "E80.0", {"start": v(-70, 90) * mm, "mid": v(-77.07, 87.07) * mm, "end": v(-80, 80) * mm});
            skLineSegment(sketch, "E80.1", {"start": v(-80, -80) * mm, "end": v(-80, 80) * mm});
            skArc(sketch, "E80.2", {"start": v(-80, -80) * mm, "mid": v(-77.07, -87.07) * mm, "end": v(-70, -90) * mm});
            skLineSegment(sketch, "E80.3", {"start": v(-70, 90) * mm, "end": v(70, 90) * mm});
            skArc(sketch, "E80.4", {"start": v(80, 80) * mm, "mid": v(77.07, 87.07) * mm, "end": v(70, 90) * mm});
            skLineSegment(sketch, "E80.5", {"start": v(80, -80) * mm, "end": v(80, 80) * mm});
            skArc(sketch, "E80.6", {"start": v(70, -90) * mm, "mid": v(77.07, -87.07) * mm, "end": v(80, -80) * mm});
            skLineSegment(sketch, "E80.7", {"start": v(-70, -90) * mm, "end": v(70, -90) * mm});
            skCircle(sketch, "E80.8", {"center": v(60, -67.5) * mm, "radius": 4 * mm});
            skCircle(sketch, "E80.9", {"center": v(-60, 67.5) * mm, "radius": 4 * mm});
            skCircle(sketch, "E80.10", {"center": v(-60, -67.5) * mm, "radius": 4 * mm});
            skArc(sketch, "E80.11", {"start": v(58.62, 51.33) * mm, "mid": v(0, 71.5) * mm, "end": v(-58.62, 51.33) * mm});
            skArc(sketch, "E80.12", {"start": v(-58.62, 51.33) * mm, "mid": v(-62.58, 46.43) * mm, "end": v(-64, 40.3) * mm});
            skLineSegment(sketch, "E80.13", {"start": v(-64, 40.3) * mm, "end": v(-64, -40.3) * mm});
            skArc(sketch, "E80.14", {"start": v(-64, -40.3) * mm, "mid": v(-62.58, -46.43) * mm, "end": v(-58.62, -51.33) * mm});
            skArc(sketch, "E80.15", {"start": v(-58.62, -51.33) * mm, "mid": v(0, -71.5) * mm, "end": v(58.62, -51.33) * mm});
            skArc(sketch, "E80.16", {"start": v(58.62, -51.33) * mm, "mid": v(62.58, -46.43) * mm, "end": v(64, -40.3) * mm});
            skLineSegment(sketch, "E80.17", {"start": v(64, 40.3) * mm, "end": v(64, -40.3) * mm});
            skArc(sketch, "E80.18", {"start": v(64, 40.3) * mm, "mid": v(62.58, 46.43) * mm, "end": v(58.62, 51.33) * mm});
            skLineSegment(sketch, "E81", {"start": v(-33, 90) * mm, "end": v(-15, 108) * mm});
            skLineSegment(sketch, "E82", {"start": v(-15, 108) * mm, "end": v(-15, 120) * mm});
            skLineSegment(sketch, "E83", {"start": v(33, 90) * mm, "end": v(15, 108) * mm});
            skLineSegment(sketch, "E84", {"start": v(15, 108) * mm, "end": v(15, 120) * mm});
            skArc(sketch, "E85", {"start": v(15, 120) * mm, "mid": v(0, 135) * mm, "end": v(-15, 120) * mm});
            skCircle(sketch, "E86", {"center": v(0, 120) * mm, "radius": 6 * mm});
            skLineSegment(sketch, "E87", {"start": v(0, 120) * mm, "end": v(0, 90) * mm, "construction": true});
            skLineSegment(sketch, "E88", {"start": v(-80, 0) * mm, "end": v(80, 0) * mm, "construction": true});
            skLineSegment(sketch, "E89.MirrorCS", {"start": v(15, -108) * mm, "end": v(15, -120) * mm});
            skLineSegment(sketch, "E90.MirrorCS", {"start": v(33, -90) * mm, "end": v(15, -108) * mm});
            skLineSegment(sketch, "E91.MirrorCS", {"start": v(-15, -108) * mm, "end": v(-15, -120) * mm});
            skLineSegment(sketch, "E92.MirrorCS", {"start": v(-33, -90) * mm, "end": v(-15, -108) * mm});
            skArc(sketch, "E93.MirrorCS", {"start": v(15, -120) * mm, "mid": v(0, -135) * mm, "end": v(-15, -120) * mm});
            skCircle(sketch, "E94.MirrorC", {"center": v(0, -120) * mm, "radius": 6 * mm});
            skLineSegment(sketch, "E95.MirrorCS", {"start": v(0, -120) * mm, "end": v(0, -90) * mm, "construction": true});
            skSolve(sketch);
        }
        {
            var Q0;
            {var subQ1=sQuery(id+"F17.wireOp",EDGE,"E81");Q0=makeQuery(id+"F17.imprint","IMPRINT",FACE,{"disambiguationData":[TD([[makeQuery(id+"F17.imprint","IMPRINT",EDGE,{"derivedFrom":subQ1}),-1.0]])]});}
            var Q1;
            {var subQ5=sQuery(id+"F17.wireOp",EDGE,"E80.0");Q1=makeQuery(id+"F17.imprint","IMPRINT",FACE,{"disambiguationData":[TD([[makeQuery(id+"F17.imprint","IMPRINT",EDGE,{"derivedFrom":subQ5}),1.0]])]});}
            var Q2;
            Q2=makeQuery(id+"F17.imprint","IMPRINT",FACE,{"disambiguationData":[TD([[makeQuery(id+"F17.imprint","IMPRINT",EDGE,{"derivedFrom":sQuery(id+"F17.wireOp",EDGE,"E89.MirrorCS")}),-1.0]])]});
            var Q3;
            Q3=makeQuery(id+"F2.opExtrude","CAP_FACE",FACE,{"disambiguationData":[OSD([sQuery(id+"F0.wireOp",EDGE,"E12"),sQuery(id+"F0.wireOp",EDGE,"E13"),sQuery(id+"F0.wireOp",EDGE,"E14"),sQuery(id+"F0.wireOp",EDGE,"E15"),sQuery(id+"F0.wireOp",EDGE,"E17.filletArc"),sQuery(id+"F0.wireOp",EDGE,"E18.filletArc"),sQuery(id+"F0.wireOp",EDGE,"E19.filletArc"),sQuery(id+"F0.wireOp",EDGE,"E20.filletArc"),sQuery(id+"F0.wireOp",EDGE,"E25.0"),sQuery(id+"F0.wireOp",EDGE,"E25.1"),sQuery(id+"F0.wireOp",EDGE,"E25.2"),sQuery(id+"F0.wireOp",EDGE,"E25.3"),sQuery(id+"F0.wireOp",EDGE,"E25.4"),sQuery(id+"F0.wireOp",EDGE,"E25.5"),sQuery(id+"F0.wireOp",EDGE,"E25.6"),sQuery(id+"F0.wireOp",EDGE,"E25.7")])],"isStart":false});
            extrude(context, id + "F18", {"entities" : qUnion([Q0, Q1, Q2]), "endBound" : BoundingType.UP_TO_SURFACE, "endBoundEntityFace" : qUnion([Q3]), "depth" : 25 * mm});
        }
    });
